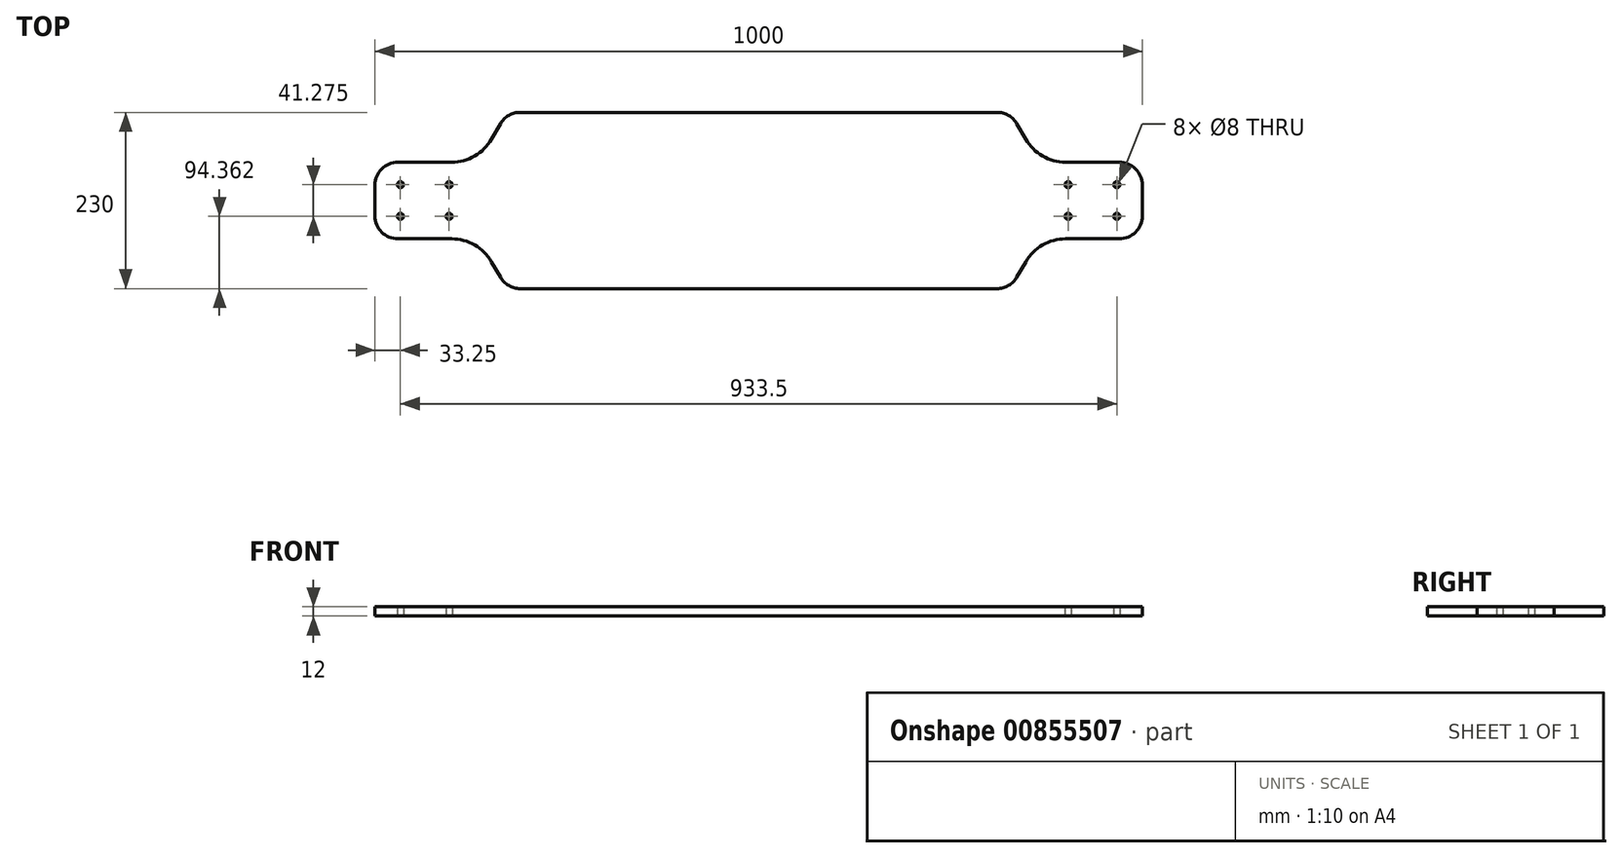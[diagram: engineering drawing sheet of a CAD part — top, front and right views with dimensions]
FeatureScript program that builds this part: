
annotation { "Feature Type Name" : "Feature", "Feature Type Description" : "" }
export const myFeature = defineFeature(function(context is Context, id is Id, definition is map)
    precondition{}
    {
        {
            var Q0;
            Q0=qCreatedBy(makeId("Top.planeOp"),FACE);
            var sketch = newSketch(context, id + "F0", { "sketchPlane" : qUnion([Q0])});
            skLineSegment(sketch, "E0", {"start": v(0, 0) * mm, "end": v(-500, 0) * mm, "construction": true});
            skLineSegment(sketch, "E1", {"start": v(-500, 0) * mm, "end": v(-500, 20) * mm});
            skLineSegment(sketch, "E2", {"start": v(-470, 50) * mm, "end": v(-400, 50) * mm});
            skLineSegment(sketch, "E3", {"start": v(-310.51, 115) * mm, "end": v(0, 115) * mm});
            skLineSegment(sketch, "E4", {"start": v(0, 0) * mm, "end": v(0, 115) * mm, "construction": true});
            skPoint(sketch, "E5.visualSharp", {"position": v(-500, 50) * mm});
            skArc(sketch, "E5.filletArc", {"start": v(-470, 50) * mm, "mid": v(-491.21, 41.21) * mm, "end": v(-500, 20) * mm});
            skPoint(sketch, "E6.visualSharp", {"position": v(-272.52, 50) * mm});
            skArc(sketch, "E6.filletArc", {"start": v(-400, 50) * mm, "mid": v(-370, 58.04) * mm, "end": v(-348.04, 80) * mm});
            skPoint(sketch, "E7.visualSharp", {"position": v(-212.97, 115) * mm});
            skLineSegment(sketch, "E8.MirrorCS", {"start": v(310.51, 115) * mm, "end": v(0, 115) * mm});
            skArc(sketch, "E9.MirrorCS", {"start": v(400, 50) * mm, "mid": v(370, 58.04) * mm, "end": v(348.04, 80) * mm});
            skLineSegment(sketch, "E10.MirrorCS", {"start": v(470, 50) * mm, "end": v(400, 50) * mm});
            skArc(sketch, "E11.MirrorCS", {"start": v(470, 50) * mm, "mid": v(491.21, 41.21) * mm, "end": v(500, 20) * mm});
            skLineSegment(sketch, "E12.MirrorCS", {"start": v(500, 0) * mm, "end": v(500, 20) * mm});
            skLineSegment(sketch, "E13.MirrorCS", {"start": v(500, 0) * mm, "end": v(500, -20) * mm});
            skArc(sketch, "E14.MirrorCS", {"start": v(470, -50) * mm, "mid": v(491.21, -41.21) * mm, "end": v(500, -20) * mm});
            skLineSegment(sketch, "E15.MirrorCS", {"start": v(470, -50) * mm, "end": v(400, -50) * mm});
            skArc(sketch, "E16.MirrorCS", {"start": v(400, -50) * mm, "mid": v(370, -58.04) * mm, "end": v(348.04, -80) * mm});
            skLineSegment(sketch, "E17.MirrorCS", {"start": v(310.51, -115) * mm, "end": v(0, -115) * mm});
            skLineSegment(sketch, "E18.MirrorCS", {"start": v(-310.51, -115) * mm, "end": v(0, -115) * mm});
            skArc(sketch, "E19.MirrorCS", {"start": v(-400, -50) * mm, "mid": v(-370, -58.04) * mm, "end": v(-348.04, -80) * mm});
            skLineSegment(sketch, "E20.MirrorCS", {"start": v(-470, -50) * mm, "end": v(-400, -50) * mm});
            skArc(sketch, "E21.MirrorCS", {"start": v(-470, -50) * mm, "mid": v(-491.21, -41.21) * mm, "end": v(-500, -20) * mm});
            skLineSegment(sketch, "E22.MirrorCS", {"start": v(-500, 0) * mm, "end": v(-500, -20) * mm});
            skLineSegment(sketch, "E23", {"start": v(500, 0) * mm, "end": v(256.45, 0) * mm, "construction": true});
            skCircle(sketch, "E24", {"center": v(466.75, 20.64) * mm, "radius": 4 * mm});
            skCircle(sketch, "E25", {"center": v(403.25, 20.64) * mm, "radius": 4 * mm});
            skLineSegment(sketch, "E26", {"start": v(466.75, 20.64) * mm, "end": v(403.25, 20.64) * mm, "construction": true});
            skLineSegment(sketch, "E27", {"start": v(435, 50) * mm, "end": v(435, 20.64) * mm, "construction": true});
            skCircle(sketch, "E28.MirrorC", {"center": v(466.75, -20.64) * mm, "radius": 4 * mm});
            skCircle(sketch, "E29.MirrorC", {"center": v(403.25, -20.64) * mm, "radius": 4 * mm});
            skCircle(sketch, "E30.MirrorC", {"center": v(-403.25, 20.64) * mm, "radius": 4 * mm});
            skCircle(sketch, "E31.MirrorC", {"center": v(-403.25, -20.64) * mm, "radius": 4 * mm});
            skCircle(sketch, "E32.MirrorC", {"center": v(-466.75, -20.64) * mm, "radius": 4 * mm});
            skCircle(sketch, "E33.MirrorC", {"center": v(-466.75, 20.64) * mm, "radius": 4 * mm});
            skLineSegment(sketch, "E34", {"start": v(-336.5, 100) * mm, "end": v(-348.04, 80) * mm});
            skPoint(sketch, "E35.visualSharp", {"position": v(-327.83, 115) * mm});
            skArc(sketch, "E35.filletArc", {"start": v(-310.51, 115) * mm, "mid": v(-325.51, 110.98) * mm, "end": v(-336.5, 100) * mm});
            skArc(sketch, "E36.MirrorCS", {"start": v(310.51, 115) * mm, "mid": v(325.51, 110.98) * mm, "end": v(336.5, 100) * mm});
            skLineSegment(sketch, "E37.MirrorCS", {"start": v(336.5, 100) * mm, "end": v(348.04, 80) * mm});
            skLineSegment(sketch, "E38.MirrorCS", {"start": v(336.5, -100) * mm, "end": v(348.04, -80) * mm});
            skArc(sketch, "E39.MirrorCS", {"start": v(310.51, -115) * mm, "mid": v(325.51, -110.98) * mm, "end": v(336.5, -100) * mm});
            skArc(sketch, "E40.MirrorCS", {"start": v(-310.51, -115) * mm, "mid": v(-325.51, -110.98) * mm, "end": v(-336.5, -100) * mm});
            skLineSegment(sketch, "E41.MirrorCS", {"start": v(-336.5, -100) * mm, "end": v(-348.04, -80) * mm});
            skPoint(sketch, "E42.orphan", {"position": v(-327.83, -115) * mm});
            skPoint(sketch, "E43.orphan", {"position": v(327.83, -115) * mm});
            skPoint(sketch, "E44.orphan", {"position": v(327.83, 115) * mm});
            skSolve(sketch);
        }
        {
            var Q0;
            Q0=makeQuery(id+"F0.imprint","IMPRINT",FACE,{"disambiguationData":[TD([[makeQuery(id+"F0.imprint","IMPRINT",EDGE,{"derivedFrom":sQuery(id+"F0.wireOp",EDGE,"E1")}),-1.0]])]});
            extrude(context, id + "F1", {"entities" : qUnion([Q0]), "depth" : 12 * mm, "offsetDistance" : 25 * mm});
        }
    });
